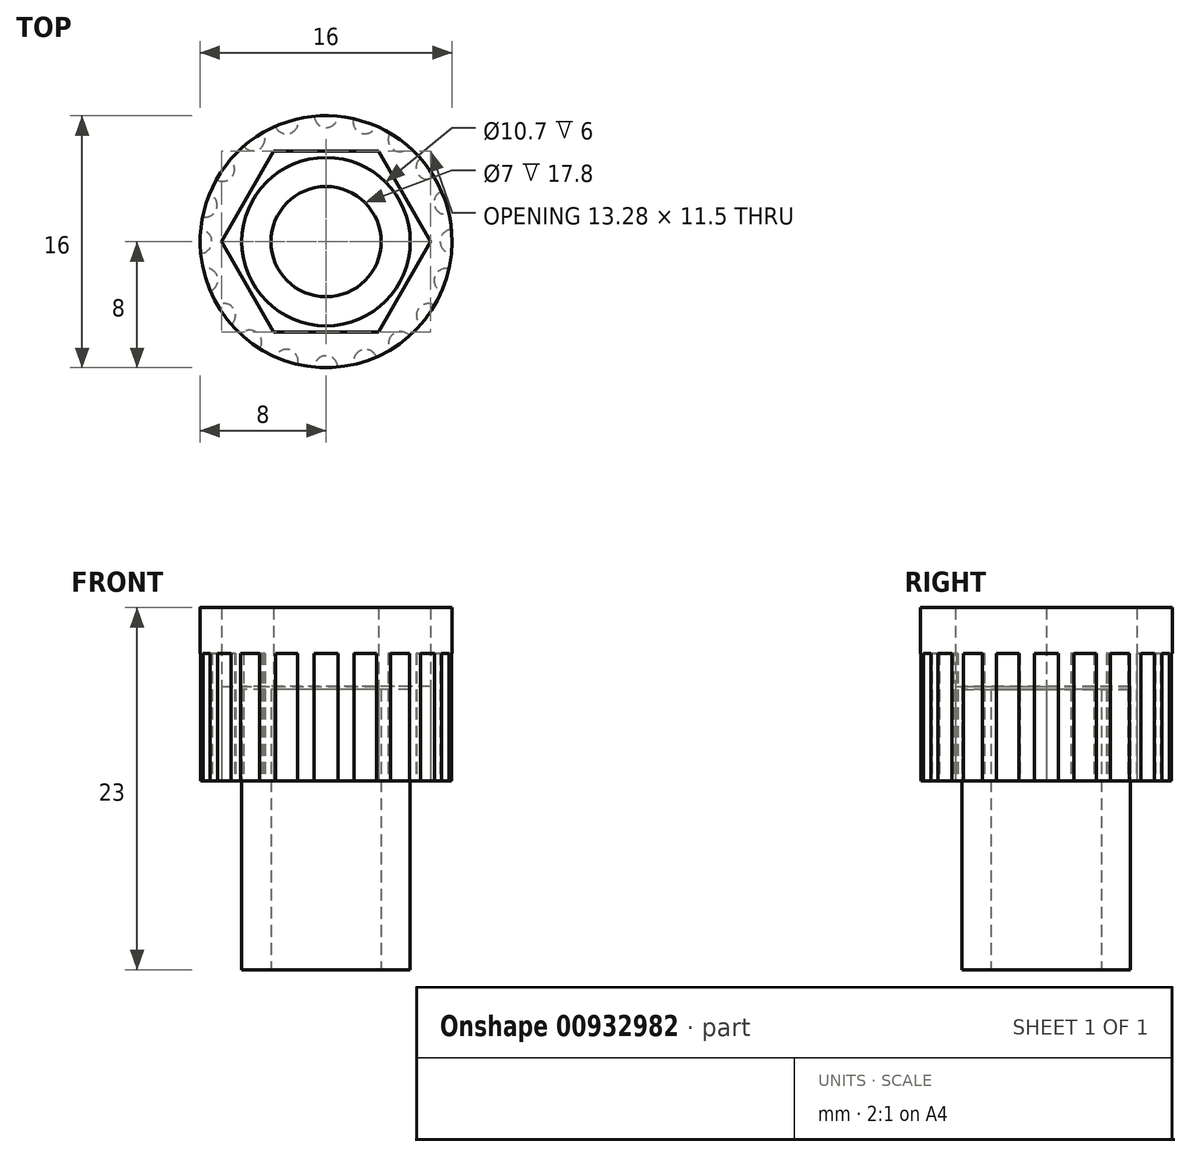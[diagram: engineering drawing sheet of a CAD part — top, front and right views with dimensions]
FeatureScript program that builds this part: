
annotation { "Feature Type Name" : "Feature", "Feature Type Description" : "" }
export const myFeature = defineFeature(function(context is Context, id is Id, definition is map)
    precondition{}
    {
        {
            var Q0;
            Q0=qCreatedBy(makeId("Top.planeOp"),FACE);
            var sketch = newSketch(context, id + "F0", { "sketchPlane" : qUnion([Q0])});
            skCircle(sketch, "E0", {"center": v(0, 0) * mm, "radius": 3.5 * mm});
            skCircle(sketch, "E1", {"center": v(0, 0) * mm, "radius": 5.35 * mm});
            skCircle(sketch, "E2", {"center": v(0, 0) * mm, "radius": 8 * mm});
            skCircle(sketch, "E3.cCircle", {"center": v(0, 0) * mm, "radius": 5.75 * mm, "construction": true});
            skLineSegment(sketch, "E3.0", {"start": v(-3.32, 5.75) * mm, "end": v(3.32, 5.75) * mm});
            skLineSegment(sketch, "E3.1", {"start": v(3.32, 5.75) * mm, "end": v(6.64, 0) * mm});
            skLineSegment(sketch, "E3.2", {"start": v(6.64, 0) * mm, "end": v(3.32, -5.75) * mm});
            skLineSegment(sketch, "E3.3", {"start": v(3.32, -5.75) * mm, "end": v(-3.32, -5.75) * mm});
            skLineSegment(sketch, "E3.4", {"start": v(-3.32, -5.75) * mm, "end": v(-6.64, 0) * mm});
            skLineSegment(sketch, "E3.5", {"start": v(-6.64, 0) * mm, "end": v(-3.32, 5.75) * mm});
            skPoint(sketch, "E3.0.midPoint", {"position": v(0, 5.75) * mm});
            skCircle(sketch, "E4", {"center": v(0, 8) * mm, "radius": 0.75 * mm});
            skCircle(sketch, "E5", {"center": v(2.47, 7.6) * mm, "radius": 0.75 * mm});
            skCircle(sketch, "E6", {"center": v(4.7, 6.48) * mm, "radius": 0.75 * mm});
            skCircle(sketch, "E7", {"center": v(6.47, 4.7) * mm, "radius": 0.75 * mm});
            skCircle(sketch, "E8", {"center": v(7.6, 2.48) * mm, "radius": 0.75 * mm});
            skCircle(sketch, "E9", {"center": v(8, 0.01) * mm, "radius": 0.75 * mm});
            skCircle(sketch, "E10", {"center": v(7.61, -2.46) * mm, "radius": 0.75 * mm});
            skCircle(sketch, "E11", {"center": v(6.48, -4.69) * mm, "radius": 0.75 * mm});
            skCircle(sketch, "E12", {"center": v(4.72, -6.46) * mm, "radius": 0.75 * mm});
            skCircle(sketch, "E13", {"center": v(2.5, -7.6) * mm, "radius": 0.75 * mm});
            skCircle(sketch, "E14", {"center": v(-2.52, -7.6) * mm, "radius": 0.75 * mm});
            skCircle(sketch, "E15", {"center": v(-4.84, -6.37) * mm, "radius": 0.75 * mm});
            skCircle(sketch, "E16", {"center": v(-6.5, -4.67) * mm, "radius": 0.75 * mm});
            skCircle(sketch, "E17", {"center": v(-7.62, -2.43) * mm, "radius": 0.75 * mm});
            skCircle(sketch, "E18", {"center": v(0, -8) * mm, "radius": 0.75 * mm});
            skCircle(sketch, "E19", {"center": v(-8, 0) * mm, "radius": 0.75 * mm});
            skCircle(sketch, "E20", {"center": v(-7.66, 2.31) * mm, "radius": 0.75 * mm});
            skCircle(sketch, "E21", {"center": v(-6.56, 4.58) * mm, "radius": 0.75 * mm});
            skCircle(sketch, "E22", {"center": v(-4.63, 6.52) * mm, "radius": 0.75 * mm});
            skCircle(sketch, "E23", {"center": v(-2.52, 7.6) * mm, "radius": 0.75 * mm});
            skSolve(sketch);
        }
        {
            var Q0;
            Q0=makeQuery(id+"F0.imprint","IMPRINT",FACE,{"disambiguationData":[TD([[makeQuery(id+"F0.imprint","IMPRINT",EDGE,{"derivedFrom":sQuery(id+"F0.wireOp",EDGE,"E0")}),-1.0]])]});
            extrude(context, id + "F1", {"entities" : qUnion([Q0]), "depth" : 18 * mm, "offsetDistance" : 25 * mm});
        }
        {
            var Q0;
            Q0=makeQuery(id+"F0.imprint","IMPRINT",FACE,{"disambiguationData":[TD([[makeQuery(id+"F0.imprint","IMPRINT",EDGE,{"derivedFrom":sQuery(id+"F0.wireOp",EDGE,"E2")}),1.0]])]});
            extrude(context, id + "F2", {"entities" : qUnion([Q0]), "depth" : 23 * mm, "offsetDistance" : 25 * mm, "hasSecondDirection" : true, "secondDirectionOppositeDirection" : false, "secondDirectionDepth" : 12 * mm});
        }
        {
            var Q0;
            Q0=makeQuery(id+"F0.imprint","IMPRINT",FACE,{"disambiguationData":[TD([[makeQuery(id+"F0.imprint","IMPRINT",EDGE,{"derivedFrom":sQuery(id+"F0.wireOp",EDGE,"E1")}),-1.0]])]});
            var Q1;
            Q1=makeQuery(id+"F0.imprint","IMPRINT",FACE,{"disambiguationData":[TD([[makeQuery(id+"F0.imprint","IMPRINT",EDGE,{"derivedFrom":sQuery(id+"F0.wireOp",EDGE,"E0")}),-1.0]])]});
            extrude(context, id + "F3", {"entities" : qUnion([Q0, Q1]), "operationType" : NewBodyOperationType.REMOVE, "depth" : 29 * mm, "offsetDistance" : 25 * mm, "hasSecondDirection" : true, "secondDirectionOppositeDirection" : false, "secondDirectionDepth" : 17.8 * mm});
        }
        {
            var Q0;
            Q0=makeQuery(id+"F0.imprint","IMPRINT",FACE,{"disambiguationData":[TD([[makeQuery(id+"F0.imprint","IMPRINT",EDGE,{"derivedFrom":sQuery(id+"F0.wireOp",EDGE,"E1")}),-1.0]])]});
            extrude(context, id + "F4", {"entities" : qUnion([Q0]), "depth" : 18 * mm, "offsetDistance" : 25 * mm, "hasSecondDirection" : true, "secondDirectionOppositeDirection" : false, "secondDirectionDepth" : 12 * mm});
        }
        {
            var Q0;
            Q0=makeQuery(id+"F0.imprint","IMPRINT",FACE,{"disambiguationData":[TD([[makeQuery(id+"F0.imprint","IMPRINT",EDGE,{"derivedFrom":sQuery(id+"F0.wireOp",EDGE,"E3.0")}),1.0]])]});
            var Q1;
            {var subQ0=sQuery(id+"F0.wireOp",EDGE,"E17");var subQ1=sQuery(id+"F0.wireOp",EDGE,"E2");var subQ2=makeQuery(id+"F0.imprint","INTERSECT",VERTEX,{"disambiguationData":[OD(0.0)],"derivedFrom":[subQ1,subQ0]});Q1=makeQuery(id+"F0.imprint","IMPRINT",FACE,{"disambiguationData":[TD([[makeQuery(id+"F0.imprint","IMPRINT",EDGE,{"disambiguationData":[TD([[subQ2,-1.0]])],"derivedFrom":subQ1}),1.0]])]});}
            var Q2;
            {var subQ0=sQuery(id+"F0.wireOp",EDGE,"E19");var subQ1=sQuery(id+"F0.wireOp",EDGE,"E2");var subQ2=makeQuery(id+"F0.imprint","INTERSECT",VERTEX,{"disambiguationData":[OD(0.0)],"derivedFrom":[subQ1,subQ0]});Q2=makeQuery(id+"F0.imprint","IMPRINT",FACE,{"disambiguationData":[TD([[makeQuery(id+"F0.imprint","IMPRINT",EDGE,{"disambiguationData":[TD([[subQ2,-1.0]])],"derivedFrom":subQ1}),1.0]])]});}
            var Q3;
            {var subQ0=sQuery(id+"F0.wireOp",EDGE,"E20");var subQ1=sQuery(id+"F0.wireOp",EDGE,"E2");var subQ2=makeQuery(id+"F0.imprint","INTERSECT",VERTEX,{"disambiguationData":[OD(0.0)],"derivedFrom":[subQ1,subQ0]});Q3=makeQuery(id+"F0.imprint","IMPRINT",FACE,{"disambiguationData":[TD([[makeQuery(id+"F0.imprint","IMPRINT",EDGE,{"disambiguationData":[TD([[subQ2,-1.0]])],"derivedFrom":subQ1}),1.0]])]});}
            var Q4;
            {var subQ0=sQuery(id+"F0.wireOp",EDGE,"E21");var subQ1=sQuery(id+"F0.wireOp",EDGE,"E2");var subQ2=makeQuery(id+"F0.imprint","INTERSECT",VERTEX,{"disambiguationData":[OD(0.0)],"derivedFrom":[subQ1,subQ0]});Q4=makeQuery(id+"F0.imprint","IMPRINT",FACE,{"disambiguationData":[TD([[makeQuery(id+"F0.imprint","IMPRINT",EDGE,{"disambiguationData":[TD([[subQ2,-1.0]])],"derivedFrom":subQ1}),1.0]])]});}
            var Q5;
            {var subQ0=sQuery(id+"F0.wireOp",EDGE,"E22");var subQ1=sQuery(id+"F0.wireOp",EDGE,"E2");var subQ2=makeQuery(id+"F0.imprint","INTERSECT",VERTEX,{"disambiguationData":[OD(0.0)],"derivedFrom":[subQ1,subQ0]});Q5=makeQuery(id+"F0.imprint","IMPRINT",FACE,{"disambiguationData":[TD([[makeQuery(id+"F0.imprint","IMPRINT",EDGE,{"disambiguationData":[TD([[subQ2,-1.0]])],"derivedFrom":subQ1}),1.0]])]});}
            var Q6;
            {var subQ0=sQuery(id+"F0.wireOp",EDGE,"E23");var subQ1=sQuery(id+"F0.wireOp",EDGE,"E2");var subQ2=makeQuery(id+"F0.imprint","INTERSECT",VERTEX,{"disambiguationData":[OD(0.0)],"derivedFrom":[subQ1,subQ0]});Q6=makeQuery(id+"F0.imprint","IMPRINT",FACE,{"disambiguationData":[TD([[makeQuery(id+"F0.imprint","IMPRINT",EDGE,{"disambiguationData":[TD([[subQ2,-1.0]])],"derivedFrom":subQ1}),1.0]])]});}
            var Q7;
            {var subQ0=sQuery(id+"F0.wireOp",EDGE,"E4");var subQ1=sQuery(id+"F0.wireOp",EDGE,"E2");var subQ2=makeQuery(id+"F0.imprint","INTERSECT",VERTEX,{"disambiguationData":[OD(0.0)],"derivedFrom":[subQ1,subQ0]});Q7=makeQuery(id+"F0.imprint","IMPRINT",FACE,{"disambiguationData":[TD([[makeQuery(id+"F0.imprint","IMPRINT",EDGE,{"disambiguationData":[TD([[subQ2,-1.0]])],"derivedFrom":subQ1}),1.0]])]});}
            var Q8;
            {var subQ0=sQuery(id+"F0.wireOp",EDGE,"E5");var subQ1=sQuery(id+"F0.wireOp",EDGE,"E2");var subQ2=makeQuery(id+"F0.imprint","INTERSECT",VERTEX,{"disambiguationData":[OD(0.0)],"derivedFrom":[subQ1,subQ0]});Q8=makeQuery(id+"F0.imprint","IMPRINT",FACE,{"disambiguationData":[TD([[makeQuery(id+"F0.imprint","IMPRINT",EDGE,{"disambiguationData":[TD([[subQ2,-1.0]])],"derivedFrom":subQ1}),1.0]])]});}
            var Q9;
            {var subQ0=sQuery(id+"F0.wireOp",EDGE,"E6");var subQ1=sQuery(id+"F0.wireOp",EDGE,"E2");var subQ2=makeQuery(id+"F0.imprint","INTERSECT",VERTEX,{"disambiguationData":[OD(0.0)],"derivedFrom":[subQ1,subQ0]});Q9=makeQuery(id+"F0.imprint","IMPRINT",FACE,{"disambiguationData":[TD([[makeQuery(id+"F0.imprint","IMPRINT",EDGE,{"disambiguationData":[TD([[subQ2,-1.0]])],"derivedFrom":subQ1}),1.0]])]});}
            var Q10;
            {var subQ0=sQuery(id+"F0.wireOp",EDGE,"E7");var subQ1=sQuery(id+"F0.wireOp",EDGE,"E2");var subQ2=makeQuery(id+"F0.imprint","INTERSECT",VERTEX,{"disambiguationData":[OD(0.0)],"derivedFrom":[subQ1,subQ0]});Q10=makeQuery(id+"F0.imprint","IMPRINT",FACE,{"disambiguationData":[TD([[makeQuery(id+"F0.imprint","IMPRINT",EDGE,{"disambiguationData":[TD([[subQ2,-1.0]])],"derivedFrom":subQ1}),1.0]])]});}
            var Q11;
            {var subQ0=sQuery(id+"F0.wireOp",EDGE,"E8");var subQ1=sQuery(id+"F0.wireOp",EDGE,"E2");var subQ2=makeQuery(id+"F0.imprint","INTERSECT",VERTEX,{"disambiguationData":[OD(0.0)],"derivedFrom":[subQ1,subQ0]});Q11=makeQuery(id+"F0.imprint","IMPRINT",FACE,{"disambiguationData":[TD([[makeQuery(id+"F0.imprint","IMPRINT",EDGE,{"disambiguationData":[TD([[subQ2,-1.0]])],"derivedFrom":subQ1}),1.0]])]});}
            var Q12;
            {var subQ0=sQuery(id+"F0.wireOp",EDGE,"E9");var subQ1=sQuery(id+"F0.wireOp",EDGE,"E2");var subQ2=makeQuery(id+"F0.imprint","INTERSECT",VERTEX,{"disambiguationData":[OD(0.0)],"derivedFrom":[subQ1,subQ0]});Q12=makeQuery(id+"F0.imprint","IMPRINT",FACE,{"disambiguationData":[TD([[makeQuery(id+"F0.imprint","IMPRINT",EDGE,{"disambiguationData":[TD([[subQ2,1.0]])],"derivedFrom":subQ1}),1.0]])]});}
            var Q13;
            {var subQ0=sQuery(id+"F0.wireOp",EDGE,"E10");var subQ1=sQuery(id+"F0.wireOp",EDGE,"E2");var subQ2=makeQuery(id+"F0.imprint","INTERSECT",VERTEX,{"disambiguationData":[OD(0.0)],"derivedFrom":[subQ1,subQ0]});Q13=makeQuery(id+"F0.imprint","IMPRINT",FACE,{"disambiguationData":[TD([[makeQuery(id+"F0.imprint","IMPRINT",EDGE,{"disambiguationData":[TD([[subQ2,-1.0]])],"derivedFrom":subQ1}),1.0]])]});}
            var Q14;
            {var subQ0=sQuery(id+"F0.wireOp",EDGE,"E11");var subQ1=sQuery(id+"F0.wireOp",EDGE,"E2");var subQ2=makeQuery(id+"F0.imprint","INTERSECT",VERTEX,{"disambiguationData":[OD(0.0)],"derivedFrom":[subQ1,subQ0]});Q14=makeQuery(id+"F0.imprint","IMPRINT",FACE,{"disambiguationData":[TD([[makeQuery(id+"F0.imprint","IMPRINT",EDGE,{"disambiguationData":[TD([[subQ2,-1.0]])],"derivedFrom":subQ1}),1.0]])]});}
            var Q15;
            {var subQ0=sQuery(id+"F0.wireOp",EDGE,"E12");var subQ1=sQuery(id+"F0.wireOp",EDGE,"E2");var subQ2=makeQuery(id+"F0.imprint","INTERSECT",VERTEX,{"disambiguationData":[OD(0.0)],"derivedFrom":[subQ1,subQ0]});Q15=makeQuery(id+"F0.imprint","IMPRINT",FACE,{"disambiguationData":[TD([[makeQuery(id+"F0.imprint","IMPRINT",EDGE,{"disambiguationData":[TD([[subQ2,-1.0]])],"derivedFrom":subQ1}),1.0]])]});}
            var Q16;
            {var subQ0=sQuery(id+"F0.wireOp",EDGE,"E13");var subQ1=sQuery(id+"F0.wireOp",EDGE,"E2");var subQ2=makeQuery(id+"F0.imprint","INTERSECT",VERTEX,{"disambiguationData":[OD(0.0)],"derivedFrom":[subQ1,subQ0]});Q16=makeQuery(id+"F0.imprint","IMPRINT",FACE,{"disambiguationData":[TD([[makeQuery(id+"F0.imprint","IMPRINT",EDGE,{"disambiguationData":[TD([[subQ2,-1.0]])],"derivedFrom":subQ1}),1.0]])]});}
            var Q17;
            {var subQ0=sQuery(id+"F0.wireOp",EDGE,"E18");var subQ1=sQuery(id+"F0.wireOp",EDGE,"E2");var subQ2=makeQuery(id+"F0.imprint","INTERSECT",VERTEX,{"disambiguationData":[OD(0.0)],"derivedFrom":[subQ1,subQ0]});Q17=makeQuery(id+"F0.imprint","IMPRINT",FACE,{"disambiguationData":[TD([[makeQuery(id+"F0.imprint","IMPRINT",EDGE,{"disambiguationData":[TD([[subQ2,-1.0]])],"derivedFrom":subQ1}),1.0]])]});}
            var Q18;
            {var subQ0=sQuery(id+"F0.wireOp",EDGE,"E14");var subQ1=sQuery(id+"F0.wireOp",EDGE,"E2");var subQ2=makeQuery(id+"F0.imprint","INTERSECT",VERTEX,{"disambiguationData":[OD(0.0)],"derivedFrom":[subQ1,subQ0]});Q18=makeQuery(id+"F0.imprint","IMPRINT",FACE,{"disambiguationData":[TD([[makeQuery(id+"F0.imprint","IMPRINT",EDGE,{"disambiguationData":[TD([[subQ2,-1.0]])],"derivedFrom":subQ1}),1.0]])]});}
            var Q19;
            {var subQ0=sQuery(id+"F0.wireOp",EDGE,"E15");var subQ1=sQuery(id+"F0.wireOp",EDGE,"E2");var subQ2=makeQuery(id+"F0.imprint","INTERSECT",VERTEX,{"disambiguationData":[OD(0.0)],"derivedFrom":[subQ1,subQ0]});Q19=makeQuery(id+"F0.imprint","IMPRINT",FACE,{"disambiguationData":[TD([[makeQuery(id+"F0.imprint","IMPRINT",EDGE,{"disambiguationData":[TD([[subQ2,-1.0]])],"derivedFrom":subQ1}),1.0]])]});}
            var Q20;
            {var subQ0=sQuery(id+"F0.wireOp",EDGE,"E16");var subQ1=sQuery(id+"F0.wireOp",EDGE,"E2");var subQ2=makeQuery(id+"F0.imprint","INTERSECT",VERTEX,{"disambiguationData":[OD(0.0)],"derivedFrom":[subQ1,subQ0]});Q20=makeQuery(id+"F0.imprint","IMPRINT",FACE,{"disambiguationData":[TD([[makeQuery(id+"F0.imprint","IMPRINT",EDGE,{"disambiguationData":[TD([[subQ2,-1.0]])],"derivedFrom":subQ1}),1.0]])]});}
            extrude(context, id + "F5", {"entities" : qUnion([Q0, Q1, Q2, Q3, Q4, Q5, Q6, Q7, Q8, Q9, Q10, Q11, Q12, Q13, Q14, Q15, Q16, Q17, Q18, Q19, Q20]), "operationType" : NewBodyOperationType.ADD, "depth" : 23 * mm, "offsetDistance" : 25 * mm, "hasSecondDirection" : true, "secondDirectionOppositeDirection" : false, "secondDirectionDepth" : 20.1 * mm});
        }
    });
